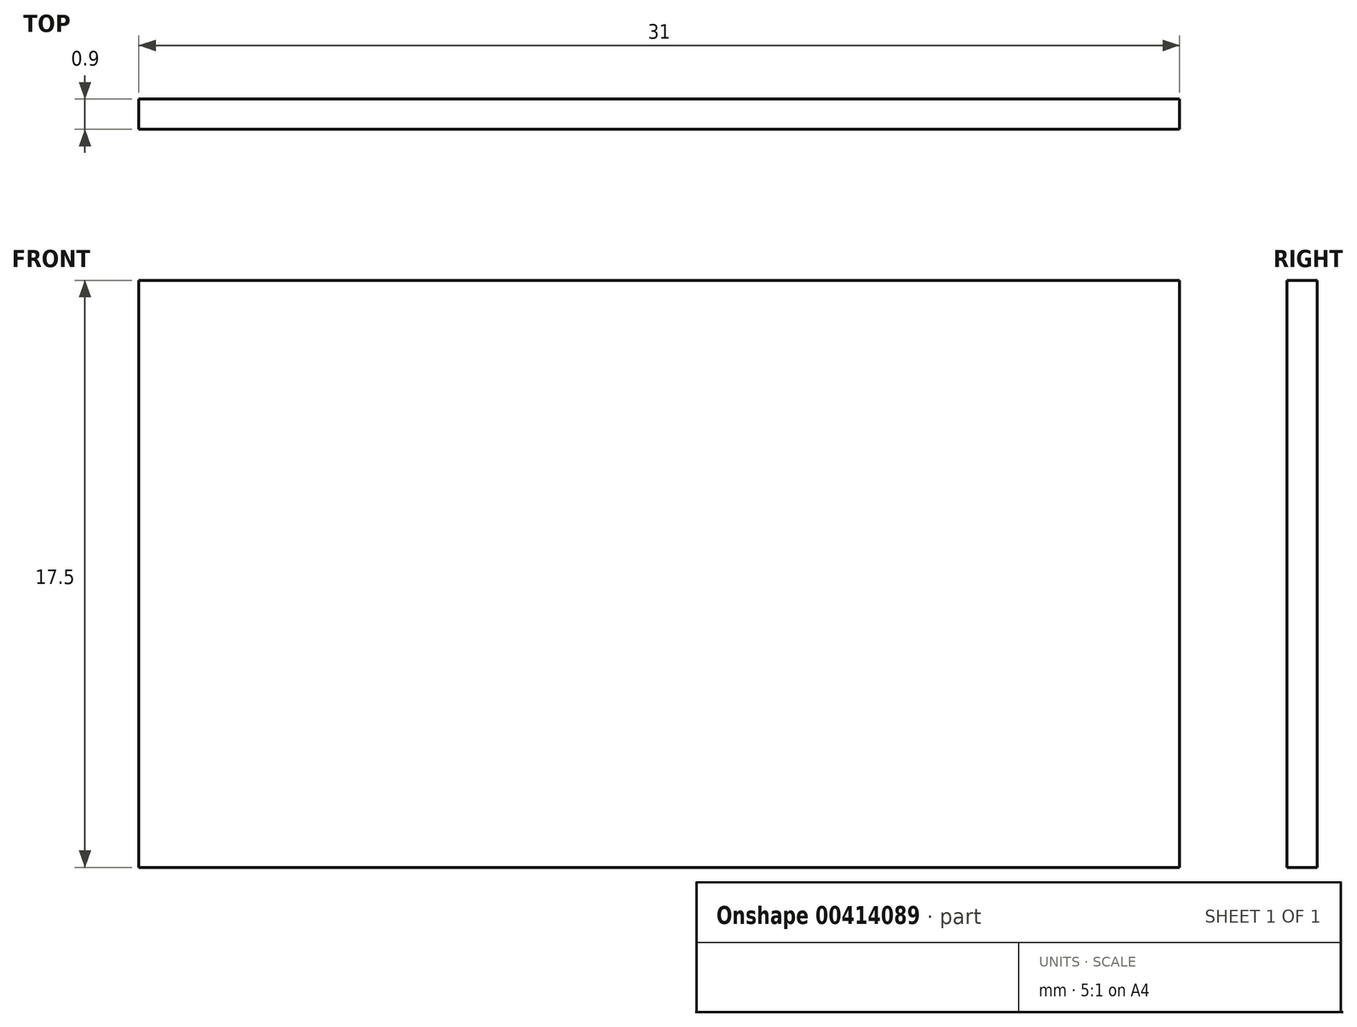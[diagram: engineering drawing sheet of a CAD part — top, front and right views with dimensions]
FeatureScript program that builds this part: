
annotation { "Feature Type Name" : "Feature", "Feature Type Description" : "" }
export const myFeature = defineFeature(function(context is Context, id is Id, definition is map)
    precondition{}
    {
        {
            var Q0;
            Q0=qCreatedBy(makeId("Front.planeOp"),FACE);
            var sketch = newSketch(context, id + "F0", { "sketchPlane" : qUnion([Q0])});
            skLineSegment(sketch, "E0.bottom", {"start": v(0, 0) * mm, "end": v(31, 0) * mm});
            skLineSegment(sketch, "E0.top", {"start": v(0, 17.5) * mm, "end": v(31, 17.5) * mm});
            skLineSegment(sketch, "E0.left", {"start": v(0, 0) * mm, "end": v(0, 17.5) * mm});
            skLineSegment(sketch, "E0.right", {"start": v(31, 0) * mm, "end": v(31, 17.5) * mm});
            skSolve(sketch);
        }
        {
            var Q0;
            Q0=makeQuery(id+"F0.imprint","IMPRINT",FACE,{"disambiguationData":[TD([[makeQuery(id+"F0.imprint","IMPRINT",EDGE,{"derivedFrom":sQuery(id+"F0.wireOp",EDGE,"E0.bottom")}),1.0]])]});
            extrude(context, id + "F1", {"entities" : qUnion([Q0]), "depth" : .9 * mm});
        }
    });
